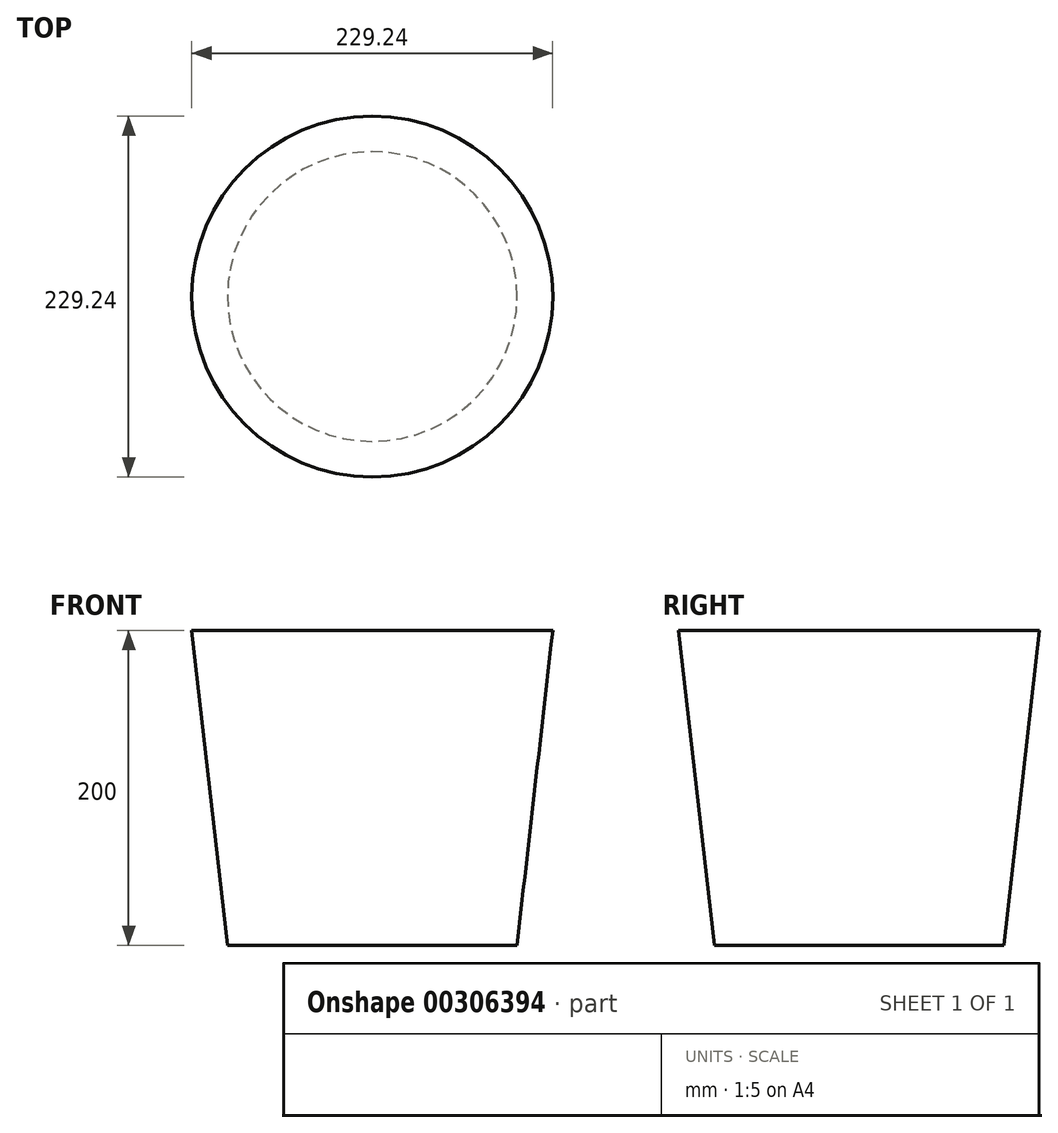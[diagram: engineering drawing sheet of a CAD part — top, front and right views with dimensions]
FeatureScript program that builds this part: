
annotation { "Feature Type Name" : "Feature", "Feature Type Description" : "" }
export const myFeature = defineFeature(function(context is Context, id is Id, definition is map)
    precondition{}
    {
        {
            var Q0;
            Q0=qCreatedBy(makeId("Front.planeOp"),FACE);
            var sketch = newSketch(context, id + "F0", { "sketchPlane" : qUnion([Q0])});
            skLineSegment(sketch, "E0", {"start": v(0, 0) * mm, "end": v(91.94, 0) * mm});
            skLineSegment(sketch, "E1", {"start": v(91.94, 0) * mm, "end": v(114.62, 200) * mm});
            skLineSegment(sketch, "E2", {"start": v(114.62, 200) * mm, "end": v(0, 200) * mm});
            skLineSegment(sketch, "E3", {"start": v(0, 200) * mm, "end": v(0, 0) * mm});
            skLineSegment(sketch, "E4", {"start": v(0, 125.97) * mm, "end": v(0, 0) * mm, "construction": true});
            skSolve(sketch);
        }
        {
            var Q0;
            Q0=makeQuery(id+"F0.imprint","IMPRINT",FACE,{"disambiguationData":[TD([[makeQuery(id+"F0.imprint","IMPRINT",EDGE,{"derivedFrom":sQuery(id+"F0.wireOp",EDGE,"E0")}),1.0]])]});
            var Q1;
            Q1=sQuery(id+"F0.wireOp",EDGE,"E3");
            revolve(context, id + "F1", {"entities" : qUnion([Q0]), "axis" : qUnion([Q1]), "revolveType" : RevolveType.FULL});
        }
    });
